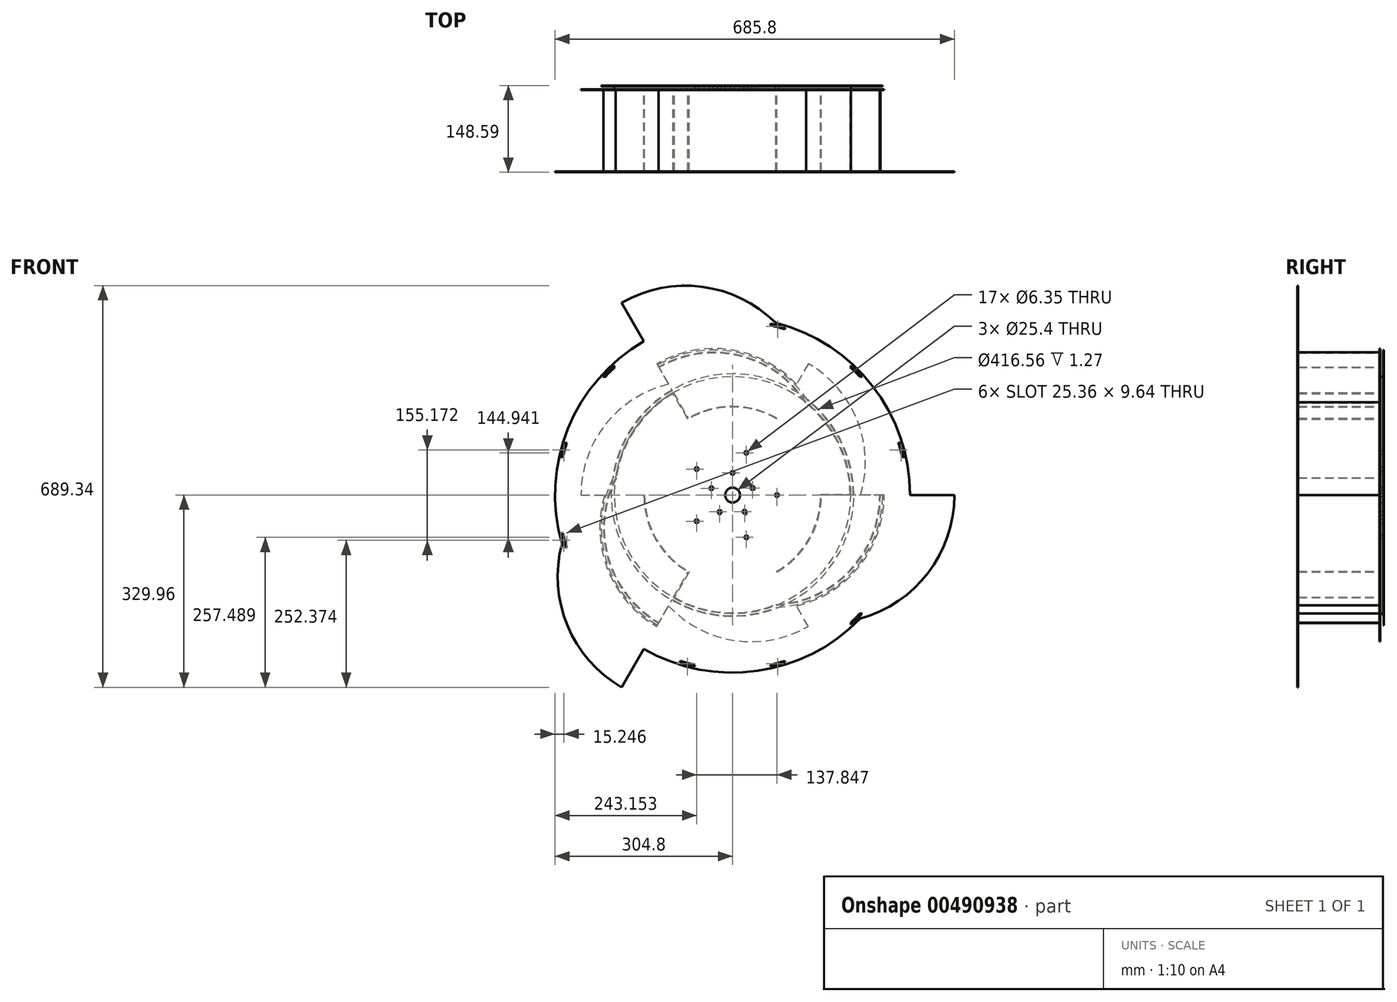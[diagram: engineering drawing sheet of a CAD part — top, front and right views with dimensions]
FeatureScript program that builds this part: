
annotation { "Feature Type Name" : "Feature", "Feature Type Description" : "" }
export const myFeature = defineFeature(function(context is Context, id is Id, definition is map)
    precondition{}
    {
        {
            var Q0;
            Q0=qCreatedBy(makeId("Front.planeOp"),FACE);
            var sketch = newSketch(context, id + "F0", { "sketchPlane" : qUnion([Q0])});
            skCircle(sketch, "E0", {"center": v(0, 0) * mm, "radius": 203.2 * mm});
            skCircle(sketch, "E1", {"center": v(0, 0) * mm, "radius": 12.7 * mm});
            skCircle(sketch, "E2", {"center": v(0, 38.1) * mm, "radius": 3.18 * mm});
            skCircle(sketch, "E3.1.0", {"center": v(-36.24, 11.77) * mm, "radius": 3.18 * mm});
            skCircle(sketch, "E3.2.0", {"center": v(-22.4, -30.82) * mm, "radius": 3.18 * mm});
            skCircle(sketch, "E3.3.0", {"center": v(22.4, -30.82) * mm, "radius": 3.18 * mm});
            skCircle(sketch, "E3.4.0", {"center": v(36.24, 11.77) * mm, "radius": 3.18 * mm});
            skLineSegment(sketch, "E4", {"start": v(0, 38.1) * mm, "end": v(36.24, 11.77) * mm, "construction": true});
            skLineSegment(sketch, "E5", {"start": v(36.24, 11.77) * mm, "end": v(22.4, -30.82) * mm, "construction": true});
            skLineSegment(sketch, "E6", {"start": v(22.4, -30.82) * mm, "end": v(-22.4, -30.82) * mm, "construction": true});
            skLineSegment(sketch, "E7", {"start": v(-22.4, -30.82) * mm, "end": v(-36.24, 11.77) * mm, "construction": true});
            skLineSegment(sketch, "E8", {"start": v(-36.24, 11.77) * mm, "end": v(0, 38.1) * mm, "construction": true});
            skSolve(sketch);
        }
        {
            var Q0;
            Q0=makeQuery(id+"F0.imprint","IMPRINT",FACE,{"disambiguationData":[TD([[makeQuery(id+"F0.imprint","IMPRINT",EDGE,{"derivedFrom":sQuery(id+"F0.wireOp",EDGE,"E0")}),1.0]])]});
            extrude(context, id + "F1", {"entities" : qUnion([Q0]), "depth" : 6.35 * mm});
        }
        {
            var Q0;
            Q0=makeQuery(id+"F1.opExtrude","CAP_FACE",FACE,{"disambiguationData":[OSD([sQuery(id+"F0.wireOp",EDGE,"E0"),sQuery(id+"F0.wireOp",EDGE,"E1"),sQuery(id+"F0.wireOp",EDGE,"E2"),sQuery(id+"F0.wireOp",EDGE,"E3.1.0"),sQuery(id+"F0.wireOp",EDGE,"E3.2.0"),sQuery(id+"F0.wireOp",EDGE,"E3.3.0"),sQuery(id+"F0.wireOp",EDGE,"E3.4.0")])],"isStart":true});
            var sketch = newSketch(context, id + "F2", { "sketchPlane" : qUnion([Q0])});
            skCircle(sketch, "E9", {"center": v(0, 0) * mm, "radius": 44.45 * mm});
            skCircle(sketch, "E10", {"center": v(0, 0) * mm, "radius": 12.7 * mm});
            skCircle(sketch, "E11", {"center": v(0, 38.1) * mm, "radius": 3.18 * mm});
            skCircle(sketch, "E12", {"center": v(36.24, 11.77) * mm, "radius": 3.18 * mm});
            skCircle(sketch, "E13", {"center": v(22.4, -30.82) * mm, "radius": 3.18 * mm});
            skCircle(sketch, "E14", {"center": v(-22.4, -30.82) * mm, "radius": 3.18 * mm});
            skCircle(sketch, "E15", {"center": v(-36.24, 11.77) * mm, "radius": 3.18 * mm});
            skSolve(sketch);
        }
        {
            var Q0;
            Q0=qSketchRegion(id+"F2",true);
            extrude(context, id + "F3", {"entities" : qUnion([Q0]), "depth" : 25.4 * mm});
        }
        {
            var Q0;
            Q0=makeQuery(id+"F3.opExtrude","CAP_FACE",FACE,{"disambiguationData":[OSD([sQuery(id+"F2.wireOp",EDGE,"E9"),sQuery(id+"F2.wireOp",EDGE,"E10"),sQuery(id+"F2.wireOp",EDGE,"E11"),sQuery(id+"F2.wireOp",EDGE,"E12"),sQuery(id+"F2.wireOp",EDGE,"E13"),sQuery(id+"F2.wireOp",EDGE,"E14"),sQuery(id+"F2.wireOp",EDGE,"E15")])],"isStart":false});
            cPlane(context, id + "F4", {"entities" : qUnion([Q0]), "cplaneType" : CPlaneType.OFFSET, "offset" : 25.4 * mm, "width" : 152.4 * mm, "height" : 152.4 * mm});
        }
        {
            var Q0;
            Q0=qCreatedBy(id+"F4.planeOp",FACE);
            var sketch = newSketch(context, id + "F5", { "sketchPlane" : qUnion([Q0])});
            skArc(sketch, "E16", {"start": v(-12.3, -3.17) * mm, "mid": v(12.7, 0) * mm, "end": v(-12.3, 3.17) * mm});
            skLineSegment(sketch, "E17", {"start": v(0, 0) * mm, "end": v(-12.7, 0) * mm, "construction": true});
            skLineSegment(sketch, "E18.bottom", {"start": v(-12.3, -3.18) * mm, "end": v(-9.76, -3.18) * mm});
            skLineSegment(sketch, "E18.top", {"start": v(-12.3, 3.17) * mm, "end": v(-9.76, 3.18) * mm});
            skLineSegment(sketch, "E18.right", {"start": v(-9.76, -3.17) * mm, "end": v(-9.76, 3.17) * mm});
            skLineSegment(sketch, "E19", {"start": v(-12.3, -3.17) * mm, "end": v(-12.3, 3.17) * mm, "construction": true});
            skSolve(sketch);
        }
        {
            var Q0;
            Q0=qSketchRegion(id+"F5",true);
            extrude(context, id + "F6", {"entities" : qUnion([Q0]), "oppositeDirection" : true, "depth" : 304.8 * mm});
        }
        {
            var Q0;
            Q0=makeQuery(id+"F1.opExtrude","CAP_FACE",FACE,{"disambiguationData":[OSD([sQuery(id+"F0.wireOp",EDGE,"E0"),sQuery(id+"F0.wireOp",EDGE,"E1"),sQuery(id+"F0.wireOp",EDGE,"E2"),sQuery(id+"F0.wireOp",EDGE,"E3.1.0"),sQuery(id+"F0.wireOp",EDGE,"E3.2.0"),sQuery(id+"F0.wireOp",EDGE,"E3.3.0"),sQuery(id+"F0.wireOp",EDGE,"E3.4.0")])],"isStart":false});
            var sketch = newSketch(context, id + "F7", { "sketchPlane" : qUnion([Q0])});
            skLineSegment(sketch, "E20", {"start": v(0, 0) * mm, "end": v(0, 203.2) * mm, "construction": true});
            skLineSegment(sketch, "E21", {"start": v(0, 203.2) * mm, "end": v(203.2, 0) * mm, "construction": true});
            skLineSegment(sketch, "E22", {"start": v(203.2, 0) * mm, "end": v(0, -203.2) * mm, "construction": true});
            skLineSegment(sketch, "E23", {"start": v(0, -203.2) * mm, "end": v(-203.2, 0) * mm, "construction": true});
            skLineSegment(sketch, "E24", {"start": v(-203.2, 0) * mm, "end": v(0, 203.2) * mm, "construction": true});
            skArc(sketch, "E25", {"start": v(0, 203.2) * mm, "mid": v(-143.68, 143.68) * mm, "end": v(-203.2, 0) * mm});
            skArc(sketch, "E26", {"start": v(0, 196.85) * mm, "mid": v(-139.2, 139.2) * mm, "end": v(-196.85, 0) * mm});
            skLineSegment(sketch, "E27", {"start": v(-203.2, 0) * mm, "end": v(-196.85, 0) * mm});
            skLineSegment(sketch, "E28", {"start": v(0, 203.2) * mm, "end": v(0, 196.85) * mm});
            skArc(sketch, "E29", {"start": v(279.4, 0) * mm, "mid": v(172.74, 147.03) * mm, "end": v(0, 203.2) * mm});
            skLineSegment(sketch, "E30", {"start": v(203.2, 0) * mm, "end": v(203.2, -92.56) * mm, "construction": true});
            skLineSegment(sketch, "E31", {"start": v(203.2, 0) * mm, "end": v(279.4, 0) * mm, "construction": true});
            skLineSegment(sketch, "E32", {"start": v(0, 203.2) * mm, "end": v(0, 209.55) * mm, "construction": true});
            skArc(sketch, "E33", {"start": v(0, 203.2) * mm, "mid": v(-38.81, 199.46) * mm, "end": v(-76.2, 188.37) * mm});
            skLineSegment(sketch, "E34", {"start": v(279.4, 0) * mm, "end": v(285.75, 0) * mm, "construction": true});
            skArc(sketch, "E35", {"start": v(285.75, 0) * mm, "mid": v(177.18, 151.55) * mm, "end": v(0, 209.55) * mm});
            skLineSegment(sketch, "E36", {"start": v(279.4, 0) * mm, "end": v(285.75, 0) * mm});
            skLineSegment(sketch, "E37", {"start": v(-76.2, 188.37) * mm, "end": v(-100.1, 178.7) * mm, "construction": true});
            skLineSegment(sketch, "E38", {"start": v(-76.2, 188.37) * mm, "end": v(-78.58, 194.26) * mm});
            skArc(sketch, "E39", {"start": v(0, 209.55) * mm, "mid": v(-40.03, 205.7) * mm, "end": v(-78.58, 194.26) * mm});
            skSolve(sketch);
        }
        {
            var Q0;
            Q0=qSketchRegion(id+"F7",true);
            extrude(context, id + "F8", {"entities" : qUnion([Q0]), "depth" : 152.4 * mm});
        }
        {
            var Q0;
            Q0=makeQuery(id+"F8.opExtrude","SWEPT_BODY",BODY,{"disambiguationData":[OSD([sQuery(id+"F7.wireOp",EDGE,"E25"),sQuery(id+"F7.wireOp",EDGE,"E26"),sQuery(id+"F7.wireOp",EDGE,"E27"),sQuery(id+"F7.wireOp",EDGE,"E28"),sQuery(id+"F7.wireOp",EDGE,"E29"),sQuery(id+"F7.wireOp",EDGE,"E35"),sQuery(id+"F7.wireOp",EDGE,"E36"),sQuery(id+"F7.wireOp",EDGE,"E38"),sQuery(id+"F7.wireOp",EDGE,"E39")])]});
            deleteBodies(context, id + "F9", {"entities" : qUnion([Q0])});
        }
        {
            var Q0;
            Q0=makeQuery(id+"F1.opExtrude","CAP_FACE",FACE,{"disambiguationData":[OSD([sQuery(id+"F0.wireOp",EDGE,"E0"),sQuery(id+"F0.wireOp",EDGE,"E1"),sQuery(id+"F0.wireOp",EDGE,"E2"),sQuery(id+"F0.wireOp",EDGE,"E3.1.0"),sQuery(id+"F0.wireOp",EDGE,"E3.2.0"),sQuery(id+"F0.wireOp",EDGE,"E3.3.0"),sQuery(id+"F0.wireOp",EDGE,"E3.4.0")])],"isStart":false});
            var sketch = newSketch(context, id + "F10", { "sketchPlane" : qUnion([Q0])});
            skLineSegment(sketch, "E40", {"start": v(0, 0) * mm, "end": v(203.2, 0) * mm, "construction": true});
            skLineSegment(sketch, "E41", {"start": v(203.2, 0) * mm, "end": v(203.2, 0) * mm});
            skLineSegment(sketch, "E42", {"start": v(203.2, 0) * mm, "end": v(524, 0) * mm, "construction": true});
            skArc(sketch, "E43", {"start": v(74.61, -189) * mm, "mid": v(202.01, -130.3) * mm, "end": v(254, 0) * mm});
            skLineSegment(sketch, "E44", {"start": v(0, 0) * mm, "end": v(-101.6, -175.98) * mm, "construction": true});
            skLineSegment(sketch, "E45", {"start": v(0, 0) * mm, "end": v(-101.6, 175.98) * mm, "construction": true});
            skLineSegment(sketch, "E46", {"start": v(-101.6, -175.98) * mm, "end": v(-76.2, -131.98) * mm});
            skArc(sketch, "E47", {"start": v(-152.4, 0) * mm, "mid": v(-131.98, -76.2) * mm, "end": v(-76.2, -131.98) * mm});
            skCircle(sketch, "E48", {"center": v(0, 0) * mm, "radius": 152.4 * mm, "construction": true});
            skLineSegment(sketch, "E49", {"start": v(-152.4, 0) * mm, "end": v(-151.13, 0) * mm});
            skArc(sketch, "E50", {"start": v(-151.13, 0) * mm, "mid": v(-130.56, -76.11) * mm, "end": v(-74.46, -131.51) * mm});
            skLineSegment(sketch, "E51", {"start": v(-74.46, -131.51) * mm, "end": v(-99.86, -175.5) * mm});
            skArc(sketch, "E52", {"start": v(74.34, -187.75) * mm, "mid": v(201.02, -129.5) * mm, "end": v(252.73, 0) * mm});
            skLineSegment(sketch, "E53", {"start": v(252.73, 0) * mm, "end": v(254, 0) * mm});
            skArc(sketch, "E54.trimOffspring", {"start": v(-101.6, 175.98) * mm, "mid": v(-182.99, -88.35) * mm, "end": v(74.61, -189) * mm, "construction": true});
            skArc(sketch, "E55", {"start": v(-99.86, -175.5) * mm, "mid": v(-14.15, -201.43) * mm, "end": v(74.34, -187.75) * mm});
            skArc(sketch, "E56", {"start": v(-101.6, -175.98) * mm, "mid": v(-14.98, -202.65) * mm, "end": v(74.61, -189) * mm});
            skArc(sketch, "E57.1.0", {"start": v(76.2, -131.98) * mm, "mid": v(131.98, -76.2) * mm, "end": v(152.4, 0) * mm});
            skArc(sketch, "E57.1.1", {"start": v(75.56, -130.88) * mm, "mid": v(131.2, -75.01) * mm, "end": v(151.12, 1.27) * mm});
            skLineSegment(sketch, "E57.1.2", {"start": v(151.12, 1.27) * mm, "end": v(201.93, 1.27) * mm});
            skArc(sketch, "E57.1.3", {"start": v(201.93, 1.27) * mm, "mid": v(181.52, 88.46) * mm, "end": v(125.43, 158.25) * mm});
            skLineSegment(sketch, "E57.1.4", {"start": v(203.2, 0) * mm, "end": v(152.4, 0) * mm});
            skArc(sketch, "E57.1.5", {"start": v(203.2, 0) * mm, "mid": v(182.99, 88.35) * mm, "end": v(126.38, 159.12) * mm});
            skArc(sketch, "E57.1.6", {"start": v(126.38, 159.12) * mm, "mid": v(11.83, 240.1) * mm, "end": v(-127, 219.97) * mm});
            skArc(sketch, "E57.1.7", {"start": v(125.43, 158.25) * mm, "mid": v(11.63, 238.84) * mm, "end": v(-126.36, 218.87) * mm});
            skLineSegment(sketch, "E57.1.8", {"start": v(-126.36, 218.87) * mm, "end": v(-127, 219.97) * mm});
            skArc(sketch, "E57.2.0", {"start": v(76.2, 131.98) * mm, "mid": v(0, 152.4) * mm, "end": v(-76.2, 131.98) * mm});
            skArc(sketch, "E57.2.1", {"start": v(75.57, 130.88) * mm, "mid": v(-0.64, 151.13) * mm, "end": v(-76.66, 130.24) * mm});
            skLineSegment(sketch, "E57.2.2", {"start": v(-76.66, 130.24) * mm, "end": v(-102.06, 174.24) * mm});
            skArc(sketch, "E57.2.3", {"start": v(-102.06, 174.24) * mm, "mid": v(-167.37, 112.97) * mm, "end": v(-199.76, 29.5) * mm});
            skLineSegment(sketch, "E57.2.4", {"start": v(-101.6, 175.98) * mm, "end": v(-76.2, 131.98) * mm});
            skArc(sketch, "E57.2.5", {"start": v(-101.6, 175.98) * mm, "mid": v(-168, 114.3) * mm, "end": v(-201, 29.89) * mm});
            skArc(sketch, "E57.2.6", {"start": v(-201, 29.89) * mm, "mid": v(-213.84, -109.8) * mm, "end": v(-127, -219.97) * mm});
            skArc(sketch, "E57.2.7", {"start": v(-199.76, 29.5) * mm, "mid": v(-212.65, -109.34) * mm, "end": v(-126.37, -218.87) * mm});
            skLineSegment(sketch, "E57.2.8", {"start": v(-126.37, -218.87) * mm, "end": v(-127, -219.97) * mm});
            skLineSegment(sketch, "E58", {"start": v(75.56, -130.88) * mm, "end": v(76.2, -131.98) * mm});
            skLineSegment(sketch, "E59", {"start": v(75.57, 130.88) * mm, "end": v(76.2, 131.98) * mm});
            skSolve(sketch);
        }
        {
            var Q0;
            Q0=qSketchRegion(id+"F10",true);
            extrude(context, id + "F11", {"entities" : qUnion([Q0]), "depth" : 139.7 * mm});
        }
        {
            var Q0;
            Q0=makeQuery(id+"F11.opExtrude","CAP_FACE",FACE,{"disambiguationData":[OSD([sQuery(id+"F10.wireOp",EDGE,"E57.2.0"),sQuery(id+"F10.wireOp",EDGE,"E57.2.1"),sQuery(id+"F10.wireOp",EDGE,"E57.2.2"),sQuery(id+"F10.wireOp",EDGE,"E57.2.3"),sQuery(id+"F10.wireOp",EDGE,"E57.2.4"),sQuery(id+"F10.wireOp",EDGE,"E57.2.5"),sQuery(id+"F10.wireOp",EDGE,"E57.2.6"),sQuery(id+"F10.wireOp",EDGE,"E57.2.7"),sQuery(id+"F10.wireOp",EDGE,"E57.2.8"),sQuery(id+"F10.wireOp",EDGE,"E59")])],"isStart":false});
            var sketch = newSketch(context, id + "F12", { "sketchPlane" : qUnion([Q0])});
            skArc(sketch, "E60", {"start": v(-152.4, -263.96) * mm, "mid": v(42.3, -301.85) * mm, "end": v(219.07, -211.92) * mm});
            skArc(sketch, "E61", {"start": v(-293.06, -83.77) * mm, "mid": v(-283.43, -224.21) * mm, "end": v(-190.5, -329.96) * mm});
            skLineSegment(sketch, "E62", {"start": v(-190.5, -329.96) * mm, "end": v(-152.4, -263.96) * mm});
            skLineSegment(sketch, "E63", {"start": v(-152.4, -263.96) * mm, "end": v(-59.03, -317.87) * mm, "construction": true});
            skArc(sketch, "E64.1.0", {"start": v(219.07, -211.92) * mm, "mid": v(335.89, -133.35) * mm, "end": v(381, 0) * mm});
            skLineSegment(sketch, "E64.1.1", {"start": v(381, 0) * mm, "end": v(304.8, 0) * mm});
            skArc(sketch, "E64.2.0", {"start": v(73.99, 295.68) * mm, "mid": v(-52.46, 357.56) * mm, "end": v(-190.5, 329.96) * mm});
            skLineSegment(sketch, "E64.2.1", {"start": v(-190.5, 329.96) * mm, "end": v(-152.4, 263.96) * mm});
            skArc(sketch, "E65.trimOffspring", {"start": v(304.8, 0) * mm, "mid": v(240.27, 187.55) * mm, "end": v(73.99, 295.68) * mm});
            skArc(sketch, "E66.trimOffspring", {"start": v(-152.4, 263.96) * mm, "mid": v(-282.56, 114.3) * mm, "end": v(-293.06, -83.77) * mm});
            skSolve(sketch);
        }
        {
            var Q0;
            Q0=qSketchRegion(id+"F12",true);
            extrude(context, id + "F13", {"entities" : qUnion([Q0]), "depth" : 1.27 * mm});
        }
        {
            var Q0;
            Q0=makeQuery(id+"F13.opExtrude","CAP_FACE",FACE,{"disambiguationData":[OSD([sQuery(id+"F12.wireOp",EDGE,"E60"),sQuery(id+"F12.wireOp",EDGE,"E61"),sQuery(id+"F12.wireOp",EDGE,"E62"),sQuery(id+"F12.wireOp",EDGE,"E64.1.0"),sQuery(id+"F12.wireOp",EDGE,"E64.1.1"),sQuery(id+"F12.wireOp",EDGE,"E64.2.0"),sQuery(id+"F12.wireOp",EDGE,"E64.2.1"),sQuery(id+"F12.wireOp",EDGE,"E65.trimOffspring"),sQuery(id+"F12.wireOp",EDGE,"E66.trimOffspring")])],"isStart":false});
            var sketch = newSketch(context, id + "F14", { "sketchPlane" : qUnion([Q0])});
            skCircle(sketch, "E67", {"center": v(0, 0) * mm, "radius": 76.2 * mm, "construction": true});
            skCircle(sketch, "E68", {"center": v(76.2, 0) * mm, "radius": 3.18 * mm});
            skCircle(sketch, "E69.1.0", {"center": v(23.55, 72.47) * mm, "radius": 3.18 * mm});
            skCircle(sketch, "E69.2.0", {"center": v(-61.65, 44.79) * mm, "radius": 3.18 * mm});
            skCircle(sketch, "E69.3.0", {"center": v(-61.65, -44.79) * mm, "radius": 3.18 * mm});
            skCircle(sketch, "E69.4.0", {"center": v(23.55, -72.47) * mm, "radius": 3.18 * mm});
            skLineSegment(sketch, "E70", {"start": v(0, 0) * mm, "end": v(0, 176.8) * mm, "construction": true});
            skCircle(sketch, "E71", {"center": v(0, 0) * mm, "radius": 12.7 * mm});
            skSolve(sketch);
        }
        {
            var Q0;
            Q0=qSketchRegion(id+"F14",true);
            extrude(context, id + "F15", {"entities" : qUnion([Q0]), "operationType" : NewBodyOperationType.REMOVE, "endBound" : BoundingType.THROUGH_ALL, "oppositeDirection" : true, "depth" : 25.4 * mm});
        }
        {
            var Q0;
            Q0=makeQuery(id+"F13.opExtrude","CAP_FACE",FACE,{"disambiguationData":[OSD([sQuery(id+"F12.wireOp",EDGE,"E60"),sQuery(id+"F12.wireOp",EDGE,"E61"),sQuery(id+"F12.wireOp",EDGE,"E62"),sQuery(id+"F12.wireOp",EDGE,"E64.1.0"),sQuery(id+"F12.wireOp",EDGE,"E64.1.1"),sQuery(id+"F12.wireOp",EDGE,"E64.2.0"),sQuery(id+"F12.wireOp",EDGE,"E64.2.1"),sQuery(id+"F12.wireOp",EDGE,"E65.trimOffspring"),sQuery(id+"F12.wireOp",EDGE,"E66.trimOffspring")])],"isStart":true});
            var sketch = newSketch(context, id + "F16", { "sketchPlane" : qUnion([Q0])});
            skCircle(sketch, "E72", {"center": v(-23.55, -72.47) * mm, "radius": 6.35 * mm});
            skCircle(sketch, "E73", {"center": v(0, 0) * mm, "radius": 76.2 * mm, "construction": true});
            skCircle(sketch, "E74.1.0", {"center": v(61.65, -44.79) * mm, "radius": 6.35 * mm});
            skCircle(sketch, "E74.2.0", {"center": v(61.65, 44.79) * mm, "radius": 6.35 * mm});
            skCircle(sketch, "E74.3.0", {"center": v(-23.55, 72.47) * mm, "radius": 6.35 * mm});
            skCircle(sketch, "E74.4.0", {"center": v(-76.2, 0) * mm, "radius": 6.35 * mm});
            skSolve(sketch);
        }
        {
            var Q0;
            Q0=makeQuery(id+"F13.opExtrude","CAP_FACE",FACE,{"disambiguationData":[OSD([sQuery(id+"F12.wireOp",EDGE,"E60"),sQuery(id+"F12.wireOp",EDGE,"E61"),sQuery(id+"F12.wireOp",EDGE,"E62"),sQuery(id+"F12.wireOp",EDGE,"E64.1.0"),sQuery(id+"F12.wireOp",EDGE,"E64.1.1"),sQuery(id+"F12.wireOp",EDGE,"E64.2.0"),sQuery(id+"F12.wireOp",EDGE,"E64.2.1"),sQuery(id+"F12.wireOp",EDGE,"E65.trimOffspring"),sQuery(id+"F12.wireOp",EDGE,"E66.trimOffspring")])],"isStart":false});
            var sketch = newSketch(context, id + "F17", { "sketchPlane" : qUnion([Q0])});
            skCircle(sketch, "E75", {"center": v(0, 0) * mm, "radius": 304.8 * mm, "construction": true});
            skLineSegment(sketch, "E76", {"start": v(0, 0) * mm, "end": v(0, 304.8) * mm, "construction": true});
            skLineSegment(sketch, "E77", {"start": v(73.99, 295.68) * mm, "end": v(213.6, 260.75) * mm, "construction": true});
            skLineSegment(sketch, "E78", {"start": v(0, 0) * mm, "end": v(215.53, 215.53) * mm, "construction": true});
            skArc(sketch, "E79", {"start": v(222.07, 204.11) * mm, "mid": v(213.28, 213.28) * mm, "end": v(204.11, 222.07) * mm});
            skPoint(sketch, "E80", {"position": v(213.28, 213.28) * mm});
            skArc(sketch, "E81", {"start": v(219.83, 201.86) * mm, "mid": v(211.04, 211.04) * mm, "end": v(201.86, 219.83) * mm});
            skPoint(sketch, "E82", {"position": v(211.04, 211.04) * mm});
            skLineSegment(sketch, "E83", {"start": v(204.11, 222.07) * mm, "end": v(201.86, 219.83) * mm});
            skLineSegment(sketch, "E84", {"start": v(222.07, 204.11) * mm, "end": v(219.83, 201.86) * mm});
            skLineSegment(sketch, "E85", {"start": v(211.04, 211.04) * mm, "end": v(233.3, 188.78) * mm, "construction": true});
            skArc(sketch, "E86.1.0", {"start": v(294.38, 65.73) * mm, "mid": v(291.35, 78.07) * mm, "end": v(287.8, 90.26) * mm});
            skPoint(sketch, "E86.1.1", {"position": v(288.28, 77.24) * mm});
            skPoint(sketch, "E86.1.2", {"position": v(291.35, 78.07) * mm});
            skArc(sketch, "E86.1.3", {"start": v(291.3, 64.9) * mm, "mid": v(288.28, 77.24) * mm, "end": v(284.73, 89.44) * mm});
            skLineSegment(sketch, "E86.1.4", {"start": v(294.38, 65.73) * mm, "end": v(291.3, 64.9) * mm});
            skLineSegment(sketch, "E86.1.5", {"start": v(287.8, 90.26) * mm, "end": v(284.73, 89.44) * mm});
            skArc(sketch, "E86.2.0", {"start": v(287.8, -90.26) * mm, "mid": v(291.35, -78.07) * mm, "end": v(294.38, -65.73) * mm, "construction": true});
            skPoint(sketch, "E86.2.1", {"position": v(288.28, -77.24) * mm});
            skPoint(sketch, "E86.2.2", {"position": v(291.35, -78.07) * mm});
            skArc(sketch, "E86.2.3", {"start": v(284.73, -89.44) * mm, "mid": v(288.28, -77.24) * mm, "end": v(291.3, -64.9) * mm, "construction": true});
            skLineSegment(sketch, "E86.2.4", {"start": v(287.8, -90.26) * mm, "end": v(284.73, -89.44) * mm, "construction": true});
            skLineSegment(sketch, "E86.2.5", {"start": v(294.38, -65.73) * mm, "end": v(291.3, -64.9) * mm, "construction": true});
            skArc(sketch, "E86.3.0", {"start": v(204.11, -222.07) * mm, "mid": v(213.28, -213.28) * mm, "end": v(222.07, -204.11) * mm});
            skPoint(sketch, "E86.3.1", {"position": v(211.04, -211.04) * mm});
            skPoint(sketch, "E86.3.2", {"position": v(213.28, -213.28) * mm});
            skArc(sketch, "E86.3.3", {"start": v(201.86, -219.83) * mm, "mid": v(211.04, -211.04) * mm, "end": v(219.83, -201.86) * mm});
            skLineSegment(sketch, "E86.3.4", {"start": v(204.11, -222.07) * mm, "end": v(201.86, -219.83) * mm});
            skLineSegment(sketch, "E86.3.5", {"start": v(222.07, -204.11) * mm, "end": v(219.83, -201.86) * mm});
            skArc(sketch, "E86.4.0", {"start": v(65.73, -294.38) * mm, "mid": v(78.07, -291.35) * mm, "end": v(90.26, -287.8) * mm});
            skPoint(sketch, "E86.4.1", {"position": v(77.24, -288.28) * mm});
            skPoint(sketch, "E86.4.2", {"position": v(78.07, -291.35) * mm});
            skArc(sketch, "E86.4.3", {"start": v(64.9, -291.3) * mm, "mid": v(77.24, -288.28) * mm, "end": v(89.44, -284.73) * mm});
            skLineSegment(sketch, "E86.4.4", {"start": v(65.73, -294.38) * mm, "end": v(64.9, -291.3) * mm});
            skLineSegment(sketch, "E86.4.5", {"start": v(90.26, -287.8) * mm, "end": v(89.44, -284.73) * mm});
            skArc(sketch, "E86.5.0", {"start": v(-90.26, -287.8) * mm, "mid": v(-78.07, -291.35) * mm, "end": v(-65.73, -294.38) * mm});
            skPoint(sketch, "E86.5.1", {"position": v(-77.24, -288.28) * mm});
            skPoint(sketch, "E86.5.2", {"position": v(-78.07, -291.35) * mm});
            skArc(sketch, "E86.5.3", {"start": v(-89.44, -284.73) * mm, "mid": v(-77.24, -288.28) * mm, "end": v(-64.9, -291.3) * mm});
            skLineSegment(sketch, "E86.5.4", {"start": v(-90.26, -287.8) * mm, "end": v(-89.44, -284.73) * mm});
            skLineSegment(sketch, "E86.5.5", {"start": v(-65.73, -294.38) * mm, "end": v(-64.9, -291.3) * mm});
            skArc(sketch, "E86.6.0", {"start": v(-222.07, -204.11) * mm, "mid": v(-213.28, -213.28) * mm, "end": v(-204.11, -222.07) * mm, "construction": true});
            skPoint(sketch, "E86.6.1", {"position": v(-211.04, -211.04) * mm});
            skPoint(sketch, "E86.6.2", {"position": v(-213.28, -213.28) * mm});
            skArc(sketch, "E86.6.3", {"start": v(-219.83, -201.86) * mm, "mid": v(-211.04, -211.04) * mm, "end": v(-201.86, -219.83) * mm, "construction": true});
            skLineSegment(sketch, "E86.6.4", {"start": v(-222.07, -204.11) * mm, "end": v(-219.83, -201.86) * mm, "construction": true});
            skLineSegment(sketch, "E86.6.5", {"start": v(-204.11, -222.07) * mm, "end": v(-201.86, -219.83) * mm, "construction": true});
            skArc(sketch, "E86.7.0", {"start": v(-294.38, -65.73) * mm, "mid": v(-291.35, -78.07) * mm, "end": v(-287.8, -90.26) * mm});
            skPoint(sketch, "E86.7.1", {"position": v(-288.28, -77.24) * mm});
            skPoint(sketch, "E86.7.2", {"position": v(-291.35, -78.07) * mm});
            skArc(sketch, "E86.7.3", {"start": v(-291.3, -64.9) * mm, "mid": v(-288.28, -77.24) * mm, "end": v(-284.73, -89.44) * mm});
            skLineSegment(sketch, "E86.7.4", {"start": v(-294.38, -65.73) * mm, "end": v(-291.3, -64.9) * mm});
            skLineSegment(sketch, "E86.7.5", {"start": v(-287.8, -90.26) * mm, "end": v(-284.73, -89.44) * mm});
            skArc(sketch, "E86.8.0", {"start": v(-287.8, 90.26) * mm, "mid": v(-291.35, 78.07) * mm, "end": v(-294.38, 65.73) * mm});
            skPoint(sketch, "E86.8.1", {"position": v(-288.28, 77.24) * mm});
            skPoint(sketch, "E86.8.2", {"position": v(-291.35, 78.07) * mm});
            skArc(sketch, "E86.8.3", {"start": v(-284.73, 89.44) * mm, "mid": v(-288.28, 77.24) * mm, "end": v(-291.3, 64.9) * mm});
            skLineSegment(sketch, "E86.8.4", {"start": v(-287.8, 90.26) * mm, "end": v(-284.73, 89.44) * mm});
            skLineSegment(sketch, "E86.8.5", {"start": v(-294.38, 65.73) * mm, "end": v(-291.3, 64.9) * mm});
            skArc(sketch, "E86.9.0", {"start": v(-204.11, 222.07) * mm, "mid": v(-213.28, 213.28) * mm, "end": v(-222.07, 204.11) * mm});
            skPoint(sketch, "E86.9.1", {"position": v(-211.04, 211.04) * mm});
            skPoint(sketch, "E86.9.2", {"position": v(-213.28, 213.28) * mm});
            skArc(sketch, "E86.9.3", {"start": v(-201.86, 219.83) * mm, "mid": v(-211.04, 211.04) * mm, "end": v(-219.83, 201.86) * mm});
            skLineSegment(sketch, "E86.9.4", {"start": v(-204.11, 222.07) * mm, "end": v(-201.86, 219.83) * mm});
            skLineSegment(sketch, "E86.9.5", {"start": v(-222.07, 204.11) * mm, "end": v(-219.83, 201.86) * mm});
            skArc(sketch, "E86.10.0", {"start": v(-65.73, 294.38) * mm, "mid": v(-78.07, 291.35) * mm, "end": v(-90.26, 287.8) * mm});
            skPoint(sketch, "E86.10.1", {"position": v(-77.24, 288.28) * mm});
            skPoint(sketch, "E86.10.2", {"position": v(-78.07, 291.35) * mm});
            skArc(sketch, "E86.10.3", {"start": v(-64.9, 291.3) * mm, "mid": v(-77.24, 288.28) * mm, "end": v(-89.44, 284.73) * mm});
            skLineSegment(sketch, "E86.10.4", {"start": v(-65.73, 294.38) * mm, "end": v(-64.9, 291.3) * mm, "construction": true});
            skLineSegment(sketch, "E86.10.5", {"start": v(-90.26, 287.8) * mm, "end": v(-89.44, 284.73) * mm, "construction": true});
            skArc(sketch, "E86.11.0", {"start": v(90.26, 287.8) * mm, "mid": v(78.07, 291.35) * mm, "end": v(65.73, 294.38) * mm});
            skPoint(sketch, "E86.11.1", {"position": v(77.24, 288.28) * mm});
            skPoint(sketch, "E86.11.2", {"position": v(78.07, 291.35) * mm});
            skArc(sketch, "E86.11.3", {"start": v(89.44, 284.73) * mm, "mid": v(77.24, 288.28) * mm, "end": v(64.9, 291.3) * mm});
            skLineSegment(sketch, "E86.11.4", {"start": v(90.26, 287.8) * mm, "end": v(89.44, 284.73) * mm});
            skLineSegment(sketch, "E86.11.5", {"start": v(65.73, 294.38) * mm, "end": v(64.9, 291.3) * mm});
            skLineSegment(sketch, "E86.anchor1", {"start": v(0, 0) * mm, "end": v(219.83, 201.86) * mm, "construction": true});
            skLineSegment(sketch, "E86.anchor2", {"start": v(0, 0) * mm, "end": v(89.44, 284.73) * mm, "construction": true});
            skLineSegment(sketch, "E87", {"start": v(0, 0) * mm, "end": v(-78.89, 294.41) * mm});
            skSolve(sketch);
        }
        {
            var Q0;
            Q0=qSketchRegion(id+"F17",true);
            extrude(context, id + "F18", {"entities" : qUnion([Q0]), "operationType" : NewBodyOperationType.REMOVE, "oppositeDirection" : true, "depth" : 25.4 * mm});
        }
        {
            var Q0;
            Q0=makeQuery(id+"F11.opExtrude","CAP_FACE",FACE,{"disambiguationData":[OSD([sQuery(id+"F10.wireOp",EDGE,"E57.2.0"),sQuery(id+"F10.wireOp",EDGE,"E57.2.1"),sQuery(id+"F10.wireOp",EDGE,"E57.2.2"),sQuery(id+"F10.wireOp",EDGE,"E57.2.3"),sQuery(id+"F10.wireOp",EDGE,"E57.2.4"),sQuery(id+"F10.wireOp",EDGE,"E57.2.5"),sQuery(id+"F10.wireOp",EDGE,"E57.2.6"),sQuery(id+"F10.wireOp",EDGE,"E57.2.7"),sQuery(id+"F10.wireOp",EDGE,"E57.2.8"),sQuery(id+"F10.wireOp",EDGE,"E59")])],"isStart":true});
            var sketch = newSketch(context, id + "F19", { "sketchPlane" : qUnion([Q0])});
            skCircle(sketch, "E88", {"center": v(0, 0) * mm, "radius": 208.28 * mm});
            skArc(sketch, "E89", {"start": v(-260.35, 0) * mm, "mid": v(-205.56, -135.77) * mm, "end": v(-71.88, -195.48) * mm});
            skLineSegment(sketch, "E90", {"start": v(-254, 0) * mm, "end": v(-413.2, 0) * mm, "construction": true});
            skLineSegment(sketch, "E91", {"start": v(-260.35, 0) * mm, "end": v(-208.28, 0) * mm});
            skLineSegment(sketch, "E92.1.0", {"start": v(-130.18, -225.47) * mm, "end": v(-104.14, -180.38) * mm});
            skArc(sketch, "E92.1.1", {"start": v(-130.17, -225.47) * mm, "mid": v(14.8, -245.9) * mm, "end": v(133.35, -160) * mm});
            skLineSegment(sketch, "E92.2.0", {"start": v(130.17, -225.47) * mm, "end": v(104.14, -180.38) * mm});
            skArc(sketch, "E92.2.1", {"start": v(130.18, -225.47) * mm, "mid": v(220.36, -110.13) * mm, "end": v(205.23, 35.5) * mm});
            skLineSegment(sketch, "E92.3.0", {"start": v(260.35, 0) * mm, "end": v(208.28, 0) * mm});
            skArc(sketch, "E92.3.1", {"start": v(260.35, 0) * mm, "mid": v(205.56, 135.77) * mm, "end": v(71.88, 195.48) * mm});
            skLineSegment(sketch, "E92.4.0", {"start": v(130.17, 225.47) * mm, "end": v(104.14, 180.38) * mm});
            skArc(sketch, "E92.4.1", {"start": v(130.17, 225.47) * mm, "mid": v(-14.8, 245.9) * mm, "end": v(-133.35, 160) * mm});
            skLineSegment(sketch, "E92.5.0", {"start": v(-130.17, 225.47) * mm, "end": v(-104.14, 180.38) * mm});
            skArc(sketch, "E92.5.1", {"start": v(-130.18, 225.47) * mm, "mid": v(-220.36, 110.13) * mm, "end": v(-205.23, -35.5) * mm});
            skSolve(sketch);
        }
        {
            var Q0;
            Q0=qSketchRegion(id+"F19",true);
            extrude(context, id + "F20", {"entities" : qUnion([Q0]), "depth" : 1.27 * mm});
        }
        {
            var Q0;
            Q0=makeQuery(id+"F20.opExtrude","CAP_FACE",FACE,{"disambiguationData":[OSD([sQuery(id+"F19.wireOp",EDGE,"E88"),sQuery(id+"F19.wireOp",EDGE,"E89"),sQuery(id+"F19.wireOp",EDGE,"E91"),sQuery(id+"F19.wireOp",EDGE,"E92.1.0"),sQuery(id+"F19.wireOp",EDGE,"E92.1.1"),sQuery(id+"F19.wireOp",EDGE,"E92.2.0"),sQuery(id+"F19.wireOp",EDGE,"E92.2.1"),sQuery(id+"F19.wireOp",EDGE,"E92.3.0"),sQuery(id+"F19.wireOp",EDGE,"E92.3.1"),sQuery(id+"F19.wireOp",EDGE,"E92.4.0"),sQuery(id+"F19.wireOp",EDGE,"E92.4.1"),sQuery(id+"F19.wireOp",EDGE,"E92.5.0"),sQuery(id+"F19.wireOp",EDGE,"E92.5.1")])],"isStart":false});
            var sketch = newSketch(context, id + "F21", { "sketchPlane" : qUnion([Q0])});
            skCircle(sketch, "E93", {"center": v(0, 0) * mm, "radius": 12.7 * mm});
            skCircle(sketch, "E94", {"center": v(36.24, 11.77) * mm, "radius": 3.18 * mm});
            skCircle(sketch, "E95.1.0", {"center": v(22.2, -28.72) * mm, "radius": 3.18 * mm});
            skCircle(sketch, "E95.2.0", {"center": v(-20.66, -28.44) * mm, "radius": 3.18 * mm});
            skCircle(sketch, "E95.3.0", {"center": v(-34.17, 12.23) * mm, "radius": 3.18 * mm});
            skCircle(sketch, "E95.4.0", {"center": v(0, 38.1) * mm, "radius": 3.18 * mm});
            skPoint(sketch, "E95.center", {"position": v(0.96, 1.33) * mm});
            skLineSegment(sketch, "E95.anchor1", {"start": v(0.96, 1.33) * mm, "end": v(36.24, 11.77) * mm, "construction": true});
            skLineSegment(sketch, "E95.anchor2", {"start": v(0.96, 1.33) * mm, "end": v(0, 38.1) * mm, "construction": true});
            skSolve(sketch);
        }
        {
            var Q0;
            Q0=qSketchRegion(id+"F21",true);
            extrude(context, id + "F22", {"entities" : qUnion([Q0]), "operationType" : NewBodyOperationType.REMOVE, "endBound" : BoundingType.THROUGH_ALL, "oppositeDirection" : true, "depth" : 25.4 * mm});
        }
        {
            var Q0;
            Q0=makeQuery(id+"F1.opExtrude","CAP_FACE",FACE,{"disambiguationData":[OSD([sQuery(id+"F0.wireOp",EDGE,"E0"),sQuery(id+"F0.wireOp",EDGE,"E1"),sQuery(id+"F0.wireOp",EDGE,"E2"),sQuery(id+"F0.wireOp",EDGE,"E3.1.0"),sQuery(id+"F0.wireOp",EDGE,"E3.2.0"),sQuery(id+"F0.wireOp",EDGE,"E3.3.0"),sQuery(id+"F0.wireOp",EDGE,"E3.4.0")])],"isStart":true});
            var sketch = newSketch(context, id + "F23", { "sketchPlane" : qUnion([Q0])});
            skArc(sketch, "E96", {"start": v(128.9, 223.27) * mm, "mid": v(-18.27, 242.38) * mm, "end": v(-135.52, 151.4) * mm});
            skLineSegment(sketch, "E97", {"start": v(126.36, 218.87) * mm, "end": v(128.9, 223.27) * mm, "construction": true});
            skLineSegment(sketch, "E98", {"start": v(128.9, 223.27) * mm, "end": v(101.6, 175.98) * mm});
            skArc(sketch, "E99", {"start": v(204.67, 31.06) * mm, "mid": v(170.98, 116.7) * mm, "end": v(103.5, 179.28) * mm});
            skArc(sketch, "E100.1.0", {"start": v(-257.81, 0) * mm, "mid": v(-200.77, -137) * mm, "end": v(-63.36, -193.07) * mm});
            skArc(sketch, "E100.2.0", {"start": v(128.9, -223.27) * mm, "mid": v(219.04, -105.37) * mm, "end": v(198.88, 41.66) * mm});
            skLineSegment(sketch, "E101.1.0", {"start": v(-257.81, 0) * mm, "end": v(-203.2, 0) * mm});
            skArc(sketch, "E101.1.1", {"start": v(-129.23, 161.72) * mm, "mid": v(-186.56, 89.72) * mm, "end": v(-207.01, 0) * mm});
            skLineSegment(sketch, "E101.2.0", {"start": v(128.9, -223.27) * mm, "end": v(101.6, -175.98) * mm});
            skArc(sketch, "E101.2.1", {"start": v(-75.43, -192.78) * mm, "mid": v(15.58, -206.42) * mm, "end": v(103.5, -179.28) * mm});
            skCircle(sketch, "E102", {"center": v(0, 0) * mm, "radius": 12.7 * mm});
            skSolve(sketch);
        }
        {
            var Q0;
            Q0=qSketchRegion(id+"F23",true);
            extrude(context, id + "F24", {"entities" : qUnion([Q0]), "depth" : 1.27 * mm});
        }
        {
            var Q0;
            Q0=makeQuery(id+"F3.opExtrude","SWEPT_BODY",BODY,{"disambiguationData":[OSD([sQuery(id+"F2.wireOp",EDGE,"E9"),sQuery(id+"F2.wireOp",EDGE,"E10"),sQuery(id+"F2.wireOp",EDGE,"E11"),sQuery(id+"F2.wireOp",EDGE,"E12"),sQuery(id+"F2.wireOp",EDGE,"E13"),sQuery(id+"F2.wireOp",EDGE,"E14"),sQuery(id+"F2.wireOp",EDGE,"E15")])]});
            deleteBodies(context, id + "F25", {"entities" : qUnion([Q0])});
        }
    });
